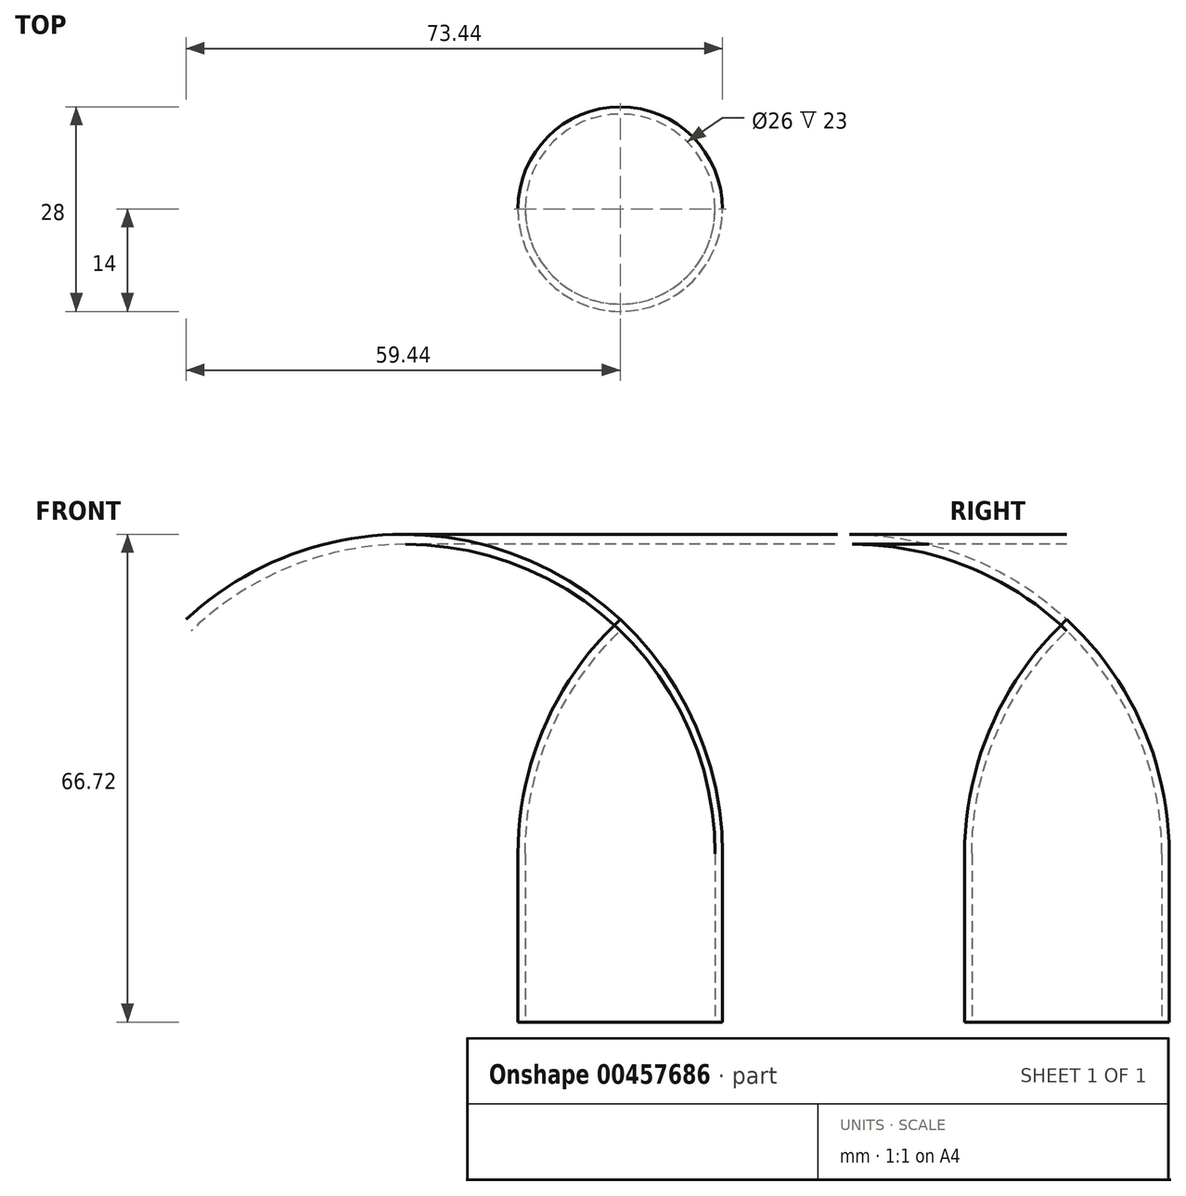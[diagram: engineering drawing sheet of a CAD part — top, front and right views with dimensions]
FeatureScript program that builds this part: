
annotation { "Feature Type Name" : "Feature", "Feature Type Description" : "" }
export const myFeature = defineFeature(function(context is Context, id is Id, definition is map)
    precondition{}
    {
        {
            var Q0;
            Q0=qCreatedBy(makeId("Front.planeOp"),FACE);
            var sketch = newSketch(context, id + "F0", { "sketchPlane" : qUnion([Q0])});
            skLineSegment(sketch, "E0", {"start": v(-13, 0) * mm, "end": v(-14, 0) * mm});
            skLineSegment(sketch, "E1", {"start": v(-14, 0) * mm, "end": v(-14, 23) * mm});
            skLineSegment(sketch, "E2", {"start": v(-13, 0) * mm, "end": v(-13, 23) * mm});
            skArc(sketch, "E3", {"start": v(0, 53.53) * mm, "mid": v(-9.61, 39.6) * mm, "end": v(-13, 23) * mm});
            skArc(sketch, "E4", {"start": v(0, 55.06) * mm, "mid": v(-10.35, 40.5) * mm, "end": v(-14, 23) * mm});
            skLineSegment(sketch, "E5", {"start": v(0, 55.06) * mm, "end": v(0, 53.53) * mm});
            skLineSegment(sketch, "E6", {"start": v(0, 0) * mm, "end": v(0, 65.9) * mm});
            skSolve(sketch);
        }
        {
            var Q0;
            Q0=makeQuery(id+"F0.imprint","IMPRINT",FACE,{"disambiguationData":[TD([[makeQuery(id+"F0.imprint","IMPRINT",EDGE,{"derivedFrom":sQuery(id+"F0.wireOp",EDGE,"E0")}),-1.0]])]});
            var Q1;
            Q1=sQuery(id+"F0.wireOp",EDGE,"E6");
            revolve(context, id + "F1", {"entities" : qUnion([Q0]), "axis" : qUnion([Q1]), "revolveType" : RevolveType.FULL});
        }
    });
